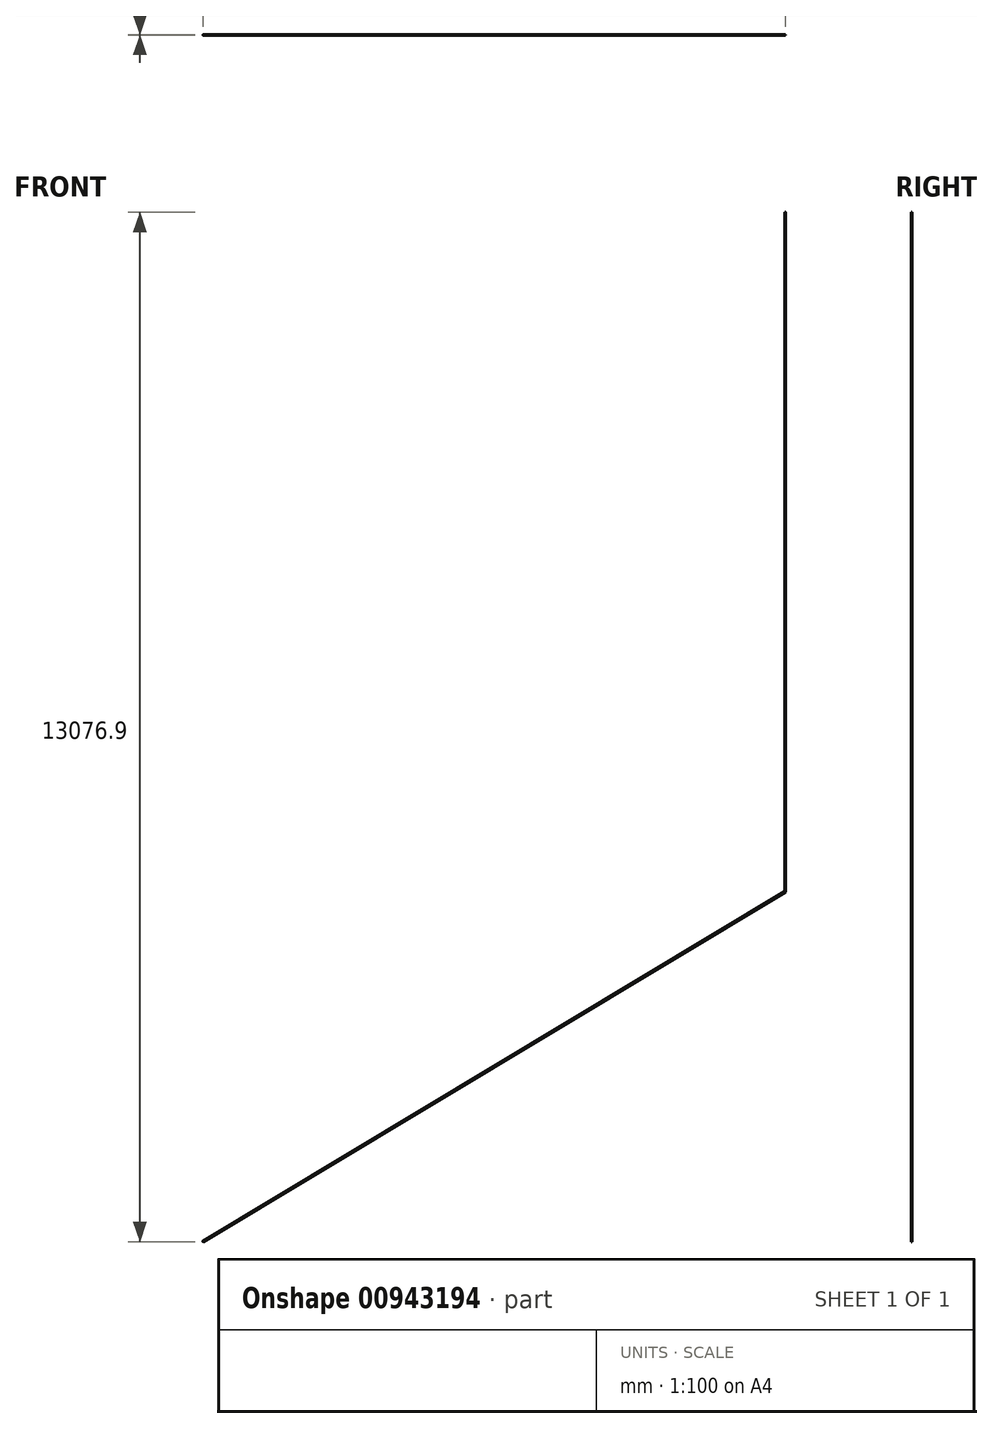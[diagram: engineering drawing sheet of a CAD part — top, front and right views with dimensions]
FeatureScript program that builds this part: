
annotation { "Feature Type Name" : "Feature", "Feature Type Description" : "" }
export const myFeature = defineFeature(function(context is Context, id is Id, definition is map)
    precondition{}
    {
        {
            var Q0;
            Q0=qCreatedBy(makeId("Top.planeOp"),FACE);
            var sketch = newSketch(context, id + "F0", { "sketchPlane" : qUnion([Q0])});
            skCircle(sketch, "E0", {"center": v(0, 0) * mm, "radius": 2.5 * mm});
            skSolve(sketch);
        }
        {
            var Q0;
            Q0=qSketchRegion(id+"F0",true);
            extrude(context, id + "F1", {"entities" : qUnion([Q0]), "depth" : 8630 * mm, "offsetDistance" : 25 * mm});
        }
        {
            var Q0;
            Q0=qCreatedBy(makeId("Top.planeOp"),FACE);
            var sketch = newSketch(context, id + "F2", { "sketchPlane" : qUnion([Q0])});
            skLineSegment(sketch, "E1", {"start": v(0, 110.68) * mm, "end": v(0, -126.57) * mm});
            skSolve(sketch);
        }
        {
            var Q0;
            Q0=makeQuery(id+"F1.opExtrude","SWEPT_BODY",BODY,{"disambiguationData":[OSD([sQuery(id+"F0.wireOp",EDGE,"E0")])]});
            var Q1;
            Q1=sQuery(id+"F2.wireOp",EDGE,"E1");
            transform(context, id + "F3", {"entities" : qUnion([Q0]), "transformType" : TransformType.ROTATION, "transformAxis" : qUnion([Q1]), "angle" : 121 * degree, "makeCopy" : true});
        }
        {
            var Q0;
            Q0=qCreatedBy(makeId("Right.planeOp"),FACE);
            var sketch = newSketch(context, id + "F4", { "sketchPlane" : qUnion([Q0])});
            skLineSegment(sketch, "E2", {"start": v(63.77, 0) * mm, "end": v(-62.94, 0) * mm});
            skSolve(sketch);
        }
        {
            var Q0;
            Q0=qCreatedBy(makeId("Right.planeOp"),FACE);
            var Q1;
            Q1=sQuery(id+"F4.wireOp",EDGE,"E2");
            cPlane(context, id + "F5", {"entities" : qUnion([Q0, Q1]), "cplaneType" : CPlaneType.LINE_ANGLE, "offset" : 25 * mm, "angle" : 60.5 * degree, "width" : 150 * mm, "height" : 150 * mm});
        }
        {
            var Q0;
            Q0=qCreatedBy(id+"F5.planeOp",FACE);
            var sketch = newSketch(context, id + "F6", { "sketchPlane" : qUnion([Q0])});
            skPoint(sketch, "E3.middle", {"position": v(0, 0) * mm});
            skCircle(sketch, "E4", {"center": v(0, 0) * mm, "radius": 2.5 * mm});
            skSolve(sketch);
        }
        {
            var Q0;
            Q0=qSketchRegion(id+"F6",true);
            extrude(context, id + "F7", {"entities" : qUnion([Q0]), "operationType" : NewBodyOperationType.ADD, "depth" : 0.01 * mm, "offsetDistance" : 25 * mm, "symmetric" : true});
        }
    });
